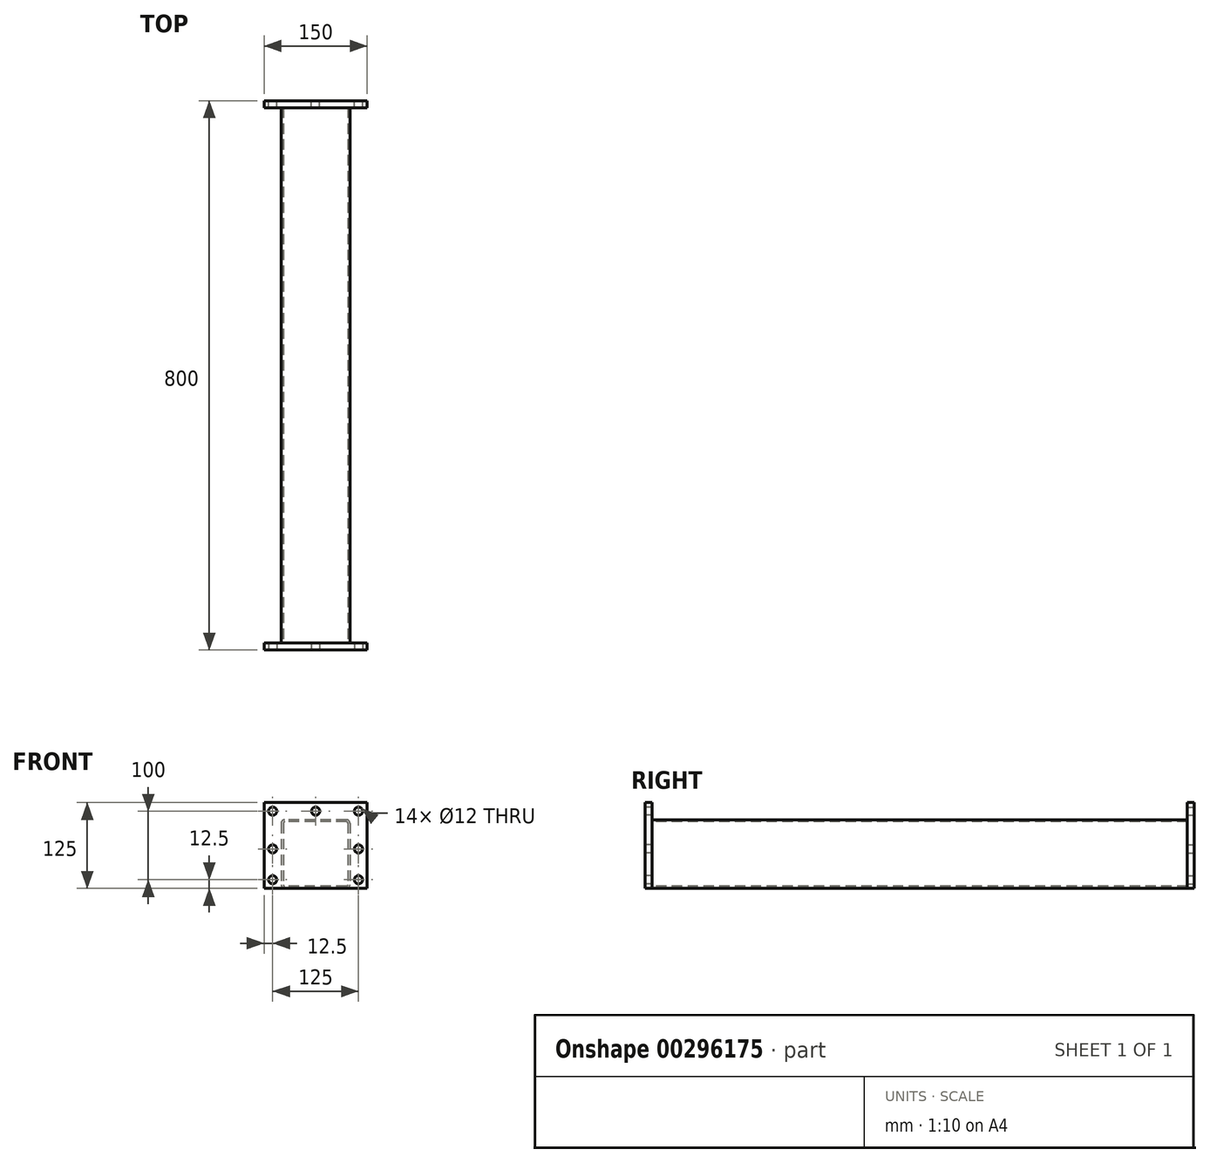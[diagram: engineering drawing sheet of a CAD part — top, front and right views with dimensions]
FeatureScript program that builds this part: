
annotation { "Feature Type Name" : "Feature", "Feature Type Description" : "" }
export const myFeature = defineFeature(function(context is Context, id is Id, definition is map)
    precondition{}
    {
        {
            var Q0;
            Q0=qCreatedBy(makeId("Front.planeOp"),FACE);
            var sketch = newSketch(context, id + "F0", { "sketchPlane" : qUnion([Q0])});
            skLineSegment(sketch, "E0.bottom", {"start": v(45, 50) * mm, "end": v(-45, 50) * mm});
            skLineSegment(sketch, "E0.top", {"start": v(45, -50) * mm, "end": v(-45, -50) * mm});
            skLineSegment(sketch, "E0.left", {"start": v(50, 45) * mm, "end": v(50, -45) * mm});
            skLineSegment(sketch, "E0.right", {"start": v(-50, 45) * mm, "end": v(-50, -45) * mm});
            skPoint(sketch, "E0.middle", {"position": v(0, 0) * mm});
            skPoint(sketch, "E1.visualSharp", {"position": v(-50, 50) * mm});
            skArc(sketch, "E1.filletArc", {"start": v(-45, 50) * mm, "mid": v(-48.54, 48.54) * mm, "end": v(-50, 45) * mm});
            skPoint(sketch, "E2.visualSharp", {"position": v(50, 50) * mm});
            skArc(sketch, "E2.filletArc", {"start": v(50, 45) * mm, "mid": v(48.54, 48.54) * mm, "end": v(45, 50) * mm});
            skPoint(sketch, "E3.visualSharp", {"position": v(50, -50) * mm});
            skArc(sketch, "E3.filletArc", {"start": v(45, -50) * mm, "mid": v(48.54, -48.54) * mm, "end": v(50, -45) * mm});
            skPoint(sketch, "E4.visualSharp", {"position": v(-50, -50) * mm});
            skArc(sketch, "E4.filletArc", {"start": v(-50, -45) * mm, "mid": v(-48.54, -48.54) * mm, "end": v(-45, -50) * mm});
            skArc(sketch, "E5.0", {"start": v(-45, 47) * mm, "mid": v(-46.41, 46.41) * mm, "end": v(-47, 45) * mm});
            skLineSegment(sketch, "E5.1", {"start": v(45, 47) * mm, "end": v(-45, 47) * mm});
            skLineSegment(sketch, "E5.2", {"start": v(-47, 45) * mm, "end": v(-47, -45) * mm});
            skArc(sketch, "E5.3", {"start": v(47, 45) * mm, "mid": v(46.41, 46.41) * mm, "end": v(45, 47) * mm});
            skArc(sketch, "E5.4", {"start": v(-47, -45) * mm, "mid": v(-46.41, -46.41) * mm, "end": v(-45, -47) * mm});
            skLineSegment(sketch, "E5.5", {"start": v(45, -47) * mm, "end": v(-45, -47) * mm});
            skArc(sketch, "E5.6", {"start": v(45, -47) * mm, "mid": v(46.41, -46.41) * mm, "end": v(47, -45) * mm});
            skLineSegment(sketch, "E5.7", {"start": v(47, 45) * mm, "end": v(47, -45) * mm});
            skSolve(sketch);
        }
        {
            var Q0;
            Q0=makeQuery(id+"F0.imprint","IMPRINT",FACE,{"disambiguationData":[TD([[makeQuery(id+"F0.imprint","IMPRINT",EDGE,{"derivedFrom":sQuery(id+"F0.wireOp",EDGE,"E0.bottom")}),1.0]])]});
            extrude(context, id + "F1", {"entities" : qUnion([Q0]), "oppositeDirection" : true, "depth" : 780 * mm});
        }
        {
            var Q0;
            Q0=makeQuery(id+"F1.opExtrude","CAP_FACE",FACE,{"disambiguationData":[OSD([sQuery(id+"F0.wireOp",EDGE,"E0.bottom"),sQuery(id+"F0.wireOp",EDGE,"E0.top"),sQuery(id+"F0.wireOp",EDGE,"E0.left"),sQuery(id+"F0.wireOp",EDGE,"E0.right"),sQuery(id+"F0.wireOp",EDGE,"E1.filletArc"),sQuery(id+"F0.wireOp",EDGE,"E2.filletArc"),sQuery(id+"F0.wireOp",EDGE,"E3.filletArc"),sQuery(id+"F0.wireOp",EDGE,"E4.filletArc"),sQuery(id+"F0.wireOp",EDGE,"E5.0"),sQuery(id+"F0.wireOp",EDGE,"E5.1"),sQuery(id+"F0.wireOp",EDGE,"E5.2"),sQuery(id+"F0.wireOp",EDGE,"E5.3"),sQuery(id+"F0.wireOp",EDGE,"E5.4"),sQuery(id+"F0.wireOp",EDGE,"E5.5"),sQuery(id+"F0.wireOp",EDGE,"E5.6"),sQuery(id+"F0.wireOp",EDGE,"E5.7")])],"isStart":true});
            cPlane(context, id + "F2", {"entities" : qUnion([Q0]), "cplaneType" : CPlaneType.OFFSET, "offset" : 10 * mm, "width" : 150 * mm, "height" : 150 * mm});
        }
        {
            var Q0;
            Q0=qCreatedBy(id+"F2.planeOp",FACE);
            var sketch = newSketch(context, id + "F3", { "sketchPlane" : qUnion([Q0])});
            skLineSegment(sketch, "E6.bottom", {"start": v(-75, 75) * mm, "end": v(75, 75) * mm});
            skLineSegment(sketch, "E6.top", {"start": v(-75, -50) * mm, "end": v(75, -50) * mm});
            skLineSegment(sketch, "E6.left", {"start": v(-75, 75) * mm, "end": v(-75, -50) * mm});
            skLineSegment(sketch, "E6.right", {"start": v(75, 75) * mm, "end": v(75, -50) * mm});
            skCircle(sketch, "E7", {"center": v(-62.5, -37.5) * mm, "radius": 6 * mm});
            skCircle(sketch, "E8", {"center": v(-62.5, 7.5) * mm, "radius": 6 * mm});
            skCircle(sketch, "E9", {"center": v(62.5, 7.5) * mm, "radius": 6 * mm});
            skCircle(sketch, "E10", {"center": v(62.5, -37.5) * mm, "radius": 6 * mm});
            skCircle(sketch, "E11", {"center": v(-62.5, 62.5) * mm, "radius": 6 * mm});
            skCircle(sketch, "E12", {"center": v(62.5, 62.5) * mm, "radius": 6 * mm});
            skCircle(sketch, "E13", {"center": v(0, 62.5) * mm, "radius": 6 * mm});
            skSolve(sketch);
        }
        {
            var Q0;
            Q0=makeQuery(id+"F3.imprint","IMPRINT",FACE,{"disambiguationData":[TD([[makeQuery(id+"F3.imprint","IMPRINT",EDGE,{"derivedFrom":sQuery(id+"F3.wireOp",EDGE,"E6.bottom")}),-1.0]])]});
            extrude(context, id + "F4", {"entities" : qUnion([Q0]), "oppositeDirection" : true, "depth" : 10 * mm});
        }
        {
            var Q0;
            Q0=makeQuery(id+"F1.opExtrude","SWEPT_BODY",BODY,{"disambiguationData":[OSD([sQuery(id+"F0.wireOp",EDGE,"E0.bottom"),sQuery(id+"F0.wireOp",EDGE,"E0.top"),sQuery(id+"F0.wireOp",EDGE,"E0.left"),sQuery(id+"F0.wireOp",EDGE,"E0.right"),sQuery(id+"F0.wireOp",EDGE,"E1.filletArc"),sQuery(id+"F0.wireOp",EDGE,"E2.filletArc"),sQuery(id+"F0.wireOp",EDGE,"E3.filletArc"),sQuery(id+"F0.wireOp",EDGE,"E4.filletArc"),sQuery(id+"F0.wireOp",EDGE,"E5.0"),sQuery(id+"F0.wireOp",EDGE,"E5.1"),sQuery(id+"F0.wireOp",EDGE,"E5.2"),sQuery(id+"F0.wireOp",EDGE,"E5.3"),sQuery(id+"F0.wireOp",EDGE,"E5.4"),sQuery(id+"F0.wireOp",EDGE,"E5.5"),sQuery(id+"F0.wireOp",EDGE,"E5.6"),sQuery(id+"F0.wireOp",EDGE,"E5.7")])]});
            var Q1;
            Q1=makeQuery(id+"F4.opExtrude","SWEPT_BODY",BODY,{"disambiguationData":[OSD([sQuery(id+"F3.wireOp",EDGE,"E6.bottom"),sQuery(id+"F3.wireOp",EDGE,"E6.top"),sQuery(id+"F3.wireOp",EDGE,"E6.left"),sQuery(id+"F3.wireOp",EDGE,"E6.right")])]});
            booleanBodies(context, id + "F5", {"operationType" : BooleanOperationType.UNION, "tools" : qUnion([Q0, Q1])});
        }
        {
            var Q0;
            Q0=makeQuery(id+"F1.opExtrude","CAP_FACE",FACE,{"disambiguationData":[OSD([sQuery(id+"F0.wireOp",EDGE,"E0.bottom"),sQuery(id+"F0.wireOp",EDGE,"E0.top"),sQuery(id+"F0.wireOp",EDGE,"E0.left"),sQuery(id+"F0.wireOp",EDGE,"E0.right"),sQuery(id+"F0.wireOp",EDGE,"E1.filletArc"),sQuery(id+"F0.wireOp",EDGE,"E2.filletArc"),sQuery(id+"F0.wireOp",EDGE,"E3.filletArc"),sQuery(id+"F0.wireOp",EDGE,"E4.filletArc"),sQuery(id+"F0.wireOp",EDGE,"E5.0"),sQuery(id+"F0.wireOp",EDGE,"E5.1"),sQuery(id+"F0.wireOp",EDGE,"E5.2"),sQuery(id+"F0.wireOp",EDGE,"E5.3"),sQuery(id+"F0.wireOp",EDGE,"E5.4"),sQuery(id+"F0.wireOp",EDGE,"E5.5"),sQuery(id+"F0.wireOp",EDGE,"E5.6"),sQuery(id+"F0.wireOp",EDGE,"E5.7")])],"isStart":false});
            cPlane(context, id + "F6", {"entities" : qUnion([Q0]), "cplaneType" : CPlaneType.OFFSET, "offset" : 10 * mm, "width" : 150 * mm, "height" : 150 * mm});
        }
        {
            var Q0;
            Q0=qCreatedBy(id+"F6.planeOp",FACE);
            var sketch = newSketch(context, id + "F7", { "sketchPlane" : qUnion([Q0])});
            skLineSegment(sketch, "E14.bottom", {"start": v(-75, 75) * mm, "end": v(75, 75) * mm});
            skLineSegment(sketch, "E14.top", {"start": v(-75, -50) * mm, "end": v(75, -50) * mm});
            skLineSegment(sketch, "E14.left", {"start": v(-75, 75) * mm, "end": v(-75, -50) * mm});
            skLineSegment(sketch, "E14.right", {"start": v(75, 75) * mm, "end": v(75, -50) * mm});
            skCircle(sketch, "E15", {"center": v(-62.5, -37.5) * mm, "radius": 6 * mm});
            skCircle(sketch, "E16", {"center": v(-62.5, 7.5) * mm, "radius": 6 * mm});
            skCircle(sketch, "E17", {"center": v(62.5, 7.5) * mm, "radius": 6 * mm});
            skCircle(sketch, "E18", {"center": v(62.5, -37.5) * mm, "radius": 6 * mm});
            skCircle(sketch, "E19", {"center": v(-62.5, 62.5) * mm, "radius": 6 * mm});
            skCircle(sketch, "E20", {"center": v(62.5, 62.5) * mm, "radius": 6 * mm});
            skCircle(sketch, "E21", {"center": v(0, 62.5) * mm, "radius": 6 * mm});
            skSolve(sketch);
        }
        {
            var Q0;
            Q0=qSketchRegion(id+"F7",true);
            extrude(context, id + "F8", {"entities" : qUnion([Q0]), "operationType" : NewBodyOperationType.ADD, "oppositeDirection" : true, "depth" : 10 * mm});
        }
    });
